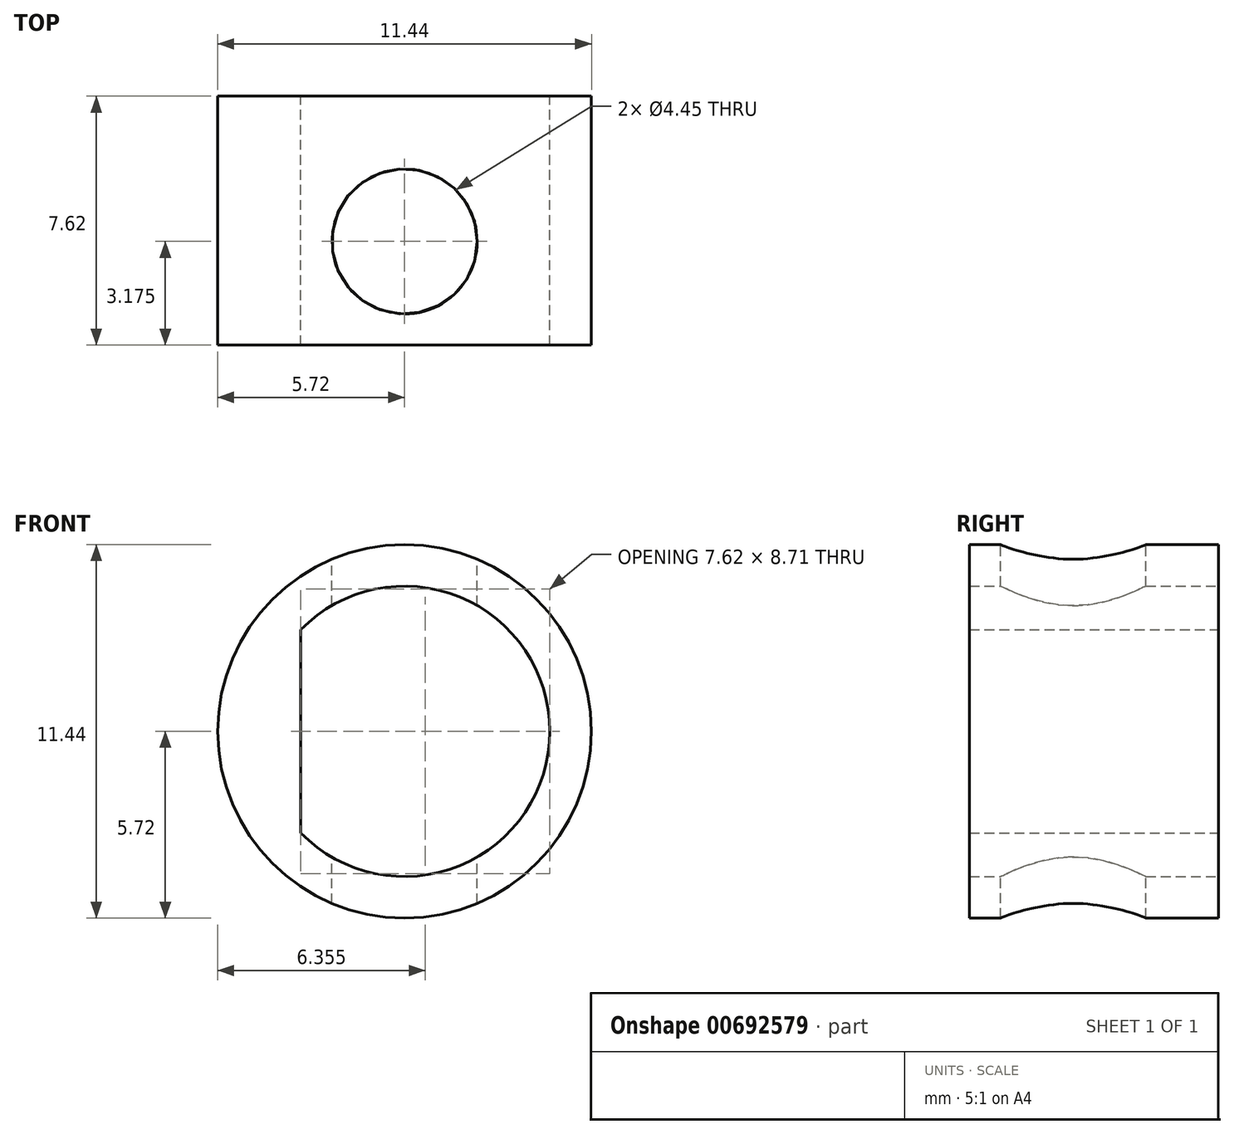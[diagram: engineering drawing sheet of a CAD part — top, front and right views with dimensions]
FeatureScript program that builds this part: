
annotation { "Feature Type Name" : "Feature", "Feature Type Description" : "" }
export const myFeature = defineFeature(function(context is Context, id is Id, definition is map)
    precondition{}
    {
        {
            var Q0;
            Q0=qCreatedBy(makeId("Front.planeOp"),FACE);
            var sketch = newSketch(context, id + "F0", { "sketchPlane" : qUnion([Q0])});
            skArc(sketch, "E0", {"start": v(-3.18, -3.11) * mm, "mid": v(4.44, 0) * mm, "end": v(-3.18, 3.11) * mm});
            skLineSegment(sketch, "E1", {"start": v(-3.18, 3.11) * mm, "end": v(-3.17, -3.11) * mm});
            skCircle(sketch, "E2", {"center": v(0, 0) * mm, "radius": 5.72 * mm});
            skSolve(sketch);
        }
        {
            var Q0;
            Q0 = qSketchRegion(id + "F0", true);
            extrude(context, id + "F1", {"entities" : qUnion([Q0]), "depth" : 7.62 * mm, "offsetDistance" : 25.4 * mm});
        }
        {
            var Q0;
            Q0=qCreatedBy(makeId("Top.planeOp"),FACE);
            var sketch = newSketch(context, id + "F2", { "sketchPlane" : qUnion([Q0])});
            skCircle(sketch, "E3", {"center": v(0, -4.45) * mm, "radius": 2.22 * mm});
            skSolve(sketch);
        }
        {
            var Q0;
            Q0=makeQuery(id+"F2.imprint","IMPRINT",FACE,{"disambiguationData":[TD([[makeQuery(id+"F2.imprint","IMPRINT",EDGE,{"derivedFrom":sQuery(id+"F2.wireOp",EDGE,"E3")}),1.0]])]});
            var Q1;
            Q1=sQuery(id+"F2.wireOp",EDGE,"E3");
            extrude(context, id + "F3", {"entities" : qUnion([Q0]), "operationType" : NewBodyOperationType.REMOVE, "surfaceEntities" : qUnion([Q1]), "endBound" : BoundingType.THROUGH_ALL, "oppositeDirection" : true, "depth" : 25.4 * mm, "offsetDistance" : 25.4 * mm, "hasSecondDirection" : true, "secondDirectionBound" : SecondDirectionBoundingType.THROUGH_ALL, "secondDirectionOppositeDirection" : false, "secondDirectionDepth" : 25.4 * mm});
        }
    });
